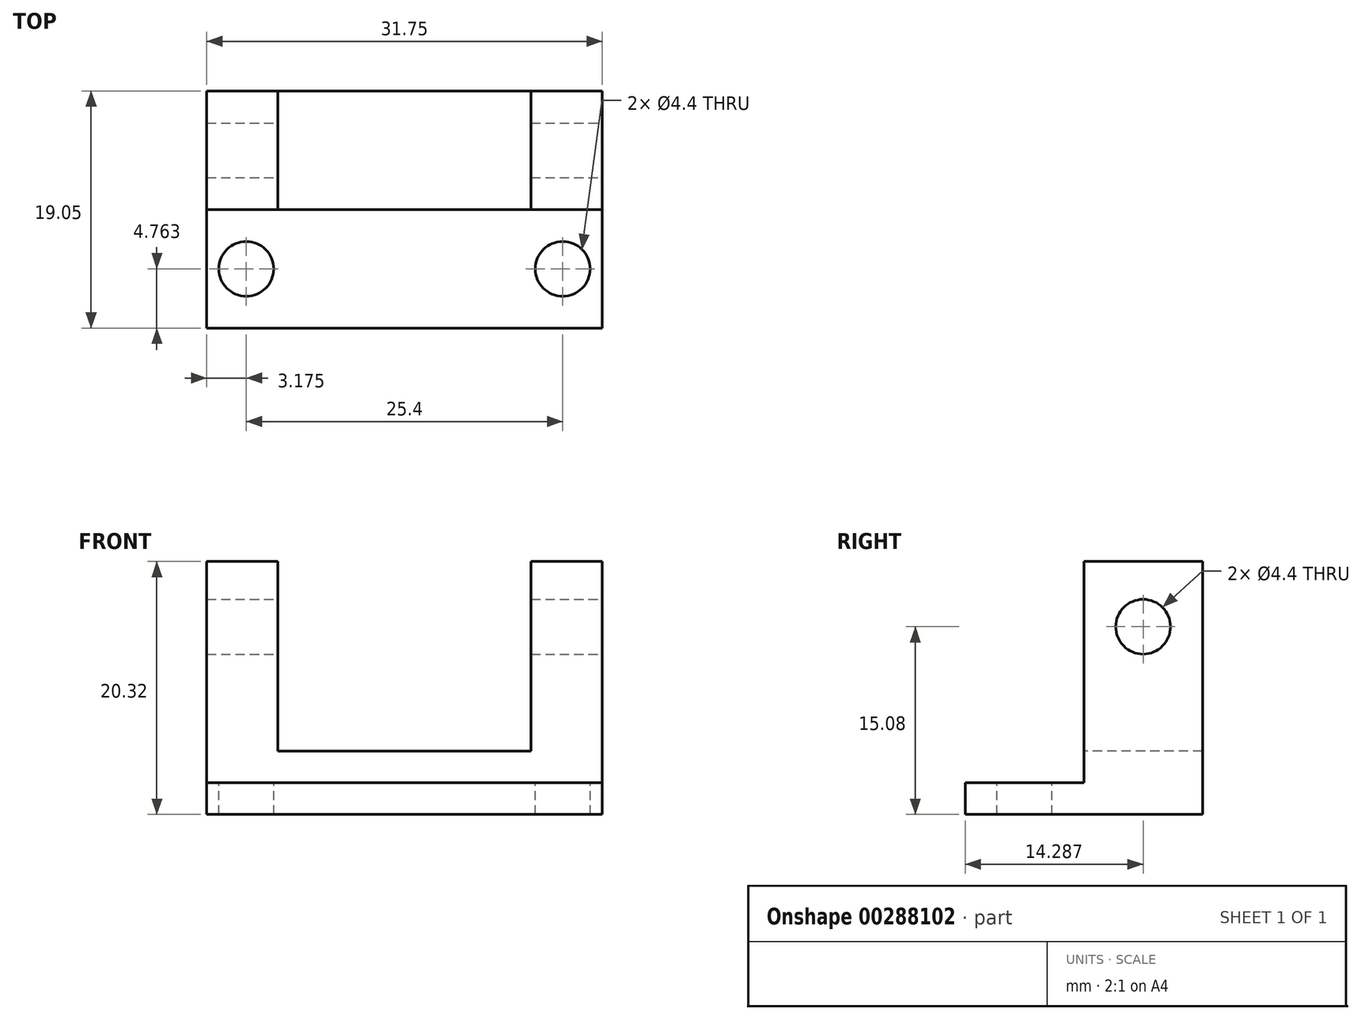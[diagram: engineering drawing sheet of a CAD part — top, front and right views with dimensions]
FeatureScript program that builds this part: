
annotation { "Feature Type Name" : "Feature", "Feature Type Description" : "" }
export const myFeature = defineFeature(function(context is Context, id is Id, definition is map)
    precondition{}
    {
        {
            var Q0;
            Q0=qCreatedBy(makeId("Top.planeOp"),FACE);
            var sketch = newSketch(context, id + "F0", { "sketchPlane" : qUnion([Q0])});
            skLineSegment(sketch, "E0.bottom", {"start": v(0, 0) * mm, "end": v(31.75, 0) * mm});
            skLineSegment(sketch, "E0.top", {"start": v(0, 19.05) * mm, "end": v(31.75, 19.05) * mm});
            skLineSegment(sketch, "E0.left", {"start": v(0, 0) * mm, "end": v(0, 19.05) * mm});
            skLineSegment(sketch, "E0.right", {"start": v(31.75, 0) * mm, "end": v(31.75, 19.05) * mm});
            skSolve(sketch);
        }
        {
            var Q0;
            Q0 = qSketchRegion(id + "F0", true);
            extrude(context, id + "F1", {"entities" : qUnion([Q0]), "depth" : 20.32 * mm});
        }
        {
            var Q0;
            Q0=makeQuery(id+"F1.opExtrude","CAP_FACE",FACE,{"disambiguationData":[OSD([sQuery(id+"F0.wireOp",EDGE,"E0.bottom"),sQuery(id+"F0.wireOp",EDGE,"E0.top"),sQuery(id+"F0.wireOp",EDGE,"E0.left"),sQuery(id+"F0.wireOp",EDGE,"E0.right")])],"isStart":false});
            var sketch = newSketch(context, id + "F2", { "sketchPlane" : qUnion([Q0])});
            skLineSegment(sketch, "E1.bottom", {"start": v(0, 0) * mm, "end": v(31.75, 0) * mm});
            skLineSegment(sketch, "E1.top", {"start": v(0, 9.53) * mm, "end": v(31.75, 9.53) * mm});
            skLineSegment(sketch, "E1.left", {"start": v(0, 0) * mm, "end": v(0, 9.53) * mm});
            skLineSegment(sketch, "E1.right", {"start": v(31.75, 0) * mm, "end": v(31.75, 9.53) * mm});
            skSolve(sketch);
        }
        {
            var Q0;
            Q0 = qSketchRegion(id + "F2", true);
            var Q1;
            Q1=makeQuery(id+"F1.opExtrude","CAP_FACE",FACE,{"disambiguationData":[OSD([sQuery(id+"F0.wireOp",EDGE,"E0.bottom"),sQuery(id+"F0.wireOp",EDGE,"E0.top"),sQuery(id+"F0.wireOp",EDGE,"E0.left"),sQuery(id+"F0.wireOp",EDGE,"E0.right")])],"isStart":true});
            var Q2;
            Q2=makeQuery(id+"F1.opExtrude","SWEPT_BODY",BODY,{"disambiguationData":[OSD([sQuery(id+"F0.wireOp",EDGE,"E0.bottom"),sQuery(id+"F0.wireOp",EDGE,"E0.top"),sQuery(id+"F0.wireOp",EDGE,"E0.left"),sQuery(id+"F0.wireOp",EDGE,"E0.right")])]});
            extrude(context, id + "F3", {"entities" : qUnion([Q0]), "operationType" : NewBodyOperationType.REMOVE, "oppositeDirection" : true, "endBoundEntityFace" : qUnion([Q1]), "endBoundEntityBody" : qUnion([Q2]), "depth" : 17.78 * mm});
        }
        {
            var Q0;
            Q0=makeQuery(id+"F1.opExtrude","CAP_FACE",FACE,{"disambiguationData":[OSD([sQuery(id+"F0.wireOp",EDGE,"E0.bottom"),sQuery(id+"F0.wireOp",EDGE,"E0.top"),sQuery(id+"F0.wireOp",EDGE,"E0.left"),sQuery(id+"F0.wireOp",EDGE,"E0.right")])],"isStart":false});
            var sketch = newSketch(context, id + "F4", { "sketchPlane" : qUnion([Q0])});
            skLineSegment(sketch, "E2.bottom", {"start": v(5.71, 19.05) * mm, "end": v(26.04, 19.05) * mm});
            skLineSegment(sketch, "E2.top", {"start": v(5.71, 9.53) * mm, "end": v(26.04, 9.53) * mm});
            skLineSegment(sketch, "E2.left", {"start": v(5.71, 19.05) * mm, "end": v(5.71, 9.53) * mm});
            skLineSegment(sketch, "E2.right", {"start": v(26.04, 19.05) * mm, "end": v(26.04, 9.53) * mm});
            skLineSegment(sketch, "E3", {"start": v(15.88, 9.53) * mm, "end": v(15.88, 19.05) * mm, "construction": true});
            skSolve(sketch);
        }
        {
            var Q0;
            Q0 = qSketchRegion(id + "F4", true);
            extrude(context, id + "F5", {"entities" : qUnion([Q0]), "operationType" : NewBodyOperationType.REMOVE, "oppositeDirection" : true, "depth" : 15.24 * mm});
        }
        {
            var Q0;
            Q0=makeQuery(id+"F3.boolean.opBoolean","COPY",FACE,{"derivedFrom":makeQuery(id+"F3.opExtrude","CAP_FACE",FACE,{"disambiguationData":[OSD([sQuery(id+"F2.wireOp",EDGE,"E1.bottom"),sQuery(id+"F2.wireOp",EDGE,"E1.top"),sQuery(id+"F2.wireOp",EDGE,"E1.left"),sQuery(id+"F2.wireOp",EDGE,"E1.right")])],"isStart":false})});
            var sketch = newSketch(context, id + "F6", { "sketchPlane" : qUnion([Q0])});
            skLineSegment(sketch, "E4", {"start": v(15.88, 9.53) * mm, "end": v(15.88, 0) * mm, "construction": true});
            skPoint(sketch, "E5", {"position": v(3.17, 4.76) * mm});
            skPoint(sketch, "E6", {"position": v(28.58, 4.76) * mm});
            skLineSegment(sketch, "E7", {"start": v(0, 4.76) * mm, "end": v(31.75, 4.76) * mm, "construction": true});
            skSolve(sketch);
        }
        {
            var Q0;
            Q0=sQuery(id+"F6.wireOp",VERTEX,"E5");
            var Q1;
            Q1=sQuery(id+"F6.wireOp",VERTEX,"E6");
            var Q2;
            Q2=makeQuery(id+"F1.opExtrude","SWEPT_BODY",BODY,{"disambiguationData":[OSD([sQuery(id+"F0.wireOp",EDGE,"E0.bottom"),sQuery(id+"F0.wireOp",EDGE,"E0.top"),sQuery(id+"F0.wireOp",EDGE,"E0.left"),sQuery(id+"F0.wireOp",EDGE,"E0.right")])]});
            hole(context, id + "F7", {"style" : HoleStyle.SIMPLE, "endStyle" : HoleEndStyle.THROUGH, "standardTappedOrClearance" : lookupTablePath({ "standard" : "ISO", "fit" : "Normal", "size" : "M4", "type" : "Clearance" }), "standardBlindInLast" : lookupTablePath({ "fit" : "Standard", "standard" : "ISO", "size" : "M4", "type" : "Clearance" }), "holeDiameter" : 4.4 * mm, "tappedDepth" : 12.7 * mm, "tapClearance" : 3, "locations" : qUnion([Q0, Q1]), "scope" : qUnion([Q2])});
        }
        {
            var Q0;
            Q0=makeQuery(id+"F1.opExtrude","SWEPT_FACE",FACE,{"disambiguationData":[OSD([sQuery(id+"F0.wireOp",EDGE,"E0.right")])]});
            var sketch = newSketch(context, id + "F8", { "sketchPlane" : qUnion([Q0])});
            skLineSegment(sketch, "E8", {"start": v(14.29, 20.32) * mm, "end": v(14.29, 0) * mm, "construction": true});
            skPoint(sketch, "E9", {"position": v(14.29, 15.08) * mm});
            skSolve(sketch);
        }
        {
            var Q0;
            Q0=sQuery(id+"F8.wireOp",VERTEX,"E9");
            var Q1;
            Q1=makeQuery(id+"F1.opExtrude","SWEPT_BODY",BODY,{"disambiguationData":[OSD([sQuery(id+"F0.wireOp",EDGE,"E0.bottom"),sQuery(id+"F0.wireOp",EDGE,"E0.top"),sQuery(id+"F0.wireOp",EDGE,"E0.left"),sQuery(id+"F0.wireOp",EDGE,"E0.right")])]});
            hole(context, id + "F9", {"style" : HoleStyle.SIMPLE, "endStyle" : HoleEndStyle.THROUGH, "standardTappedOrClearance" : lookupTablePath({ "standard" : "ISO", "fit" : "Normal", "size" : "M4", "type" : "Clearance" }), "standardBlindInLast" : lookupTablePath({ "fit" : "Standard", "standard" : "ISO", "size" : "M4", "type" : "Clearance" }), "holeDiameter" : 4.4 * mm, "tappedDepth" : 12.7 * mm, "tapClearance" : 3, "locations" : qUnion([Q0]), "scope" : qUnion([Q1])});
        }
    });
